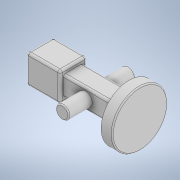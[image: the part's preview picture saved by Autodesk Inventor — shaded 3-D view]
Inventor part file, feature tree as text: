
AUTODESK INVENTOR PART (.ipt)
format: ipt  version: 2021 (Build 250183000, 183)  size: 179,712 bytes
history: native  units: in
note: dims shown in document units (in); Inventor stores cm internally (conversion verified against a paired STEP export)
features: extrude x4, sketch x4, fillet x3, plane x2
ambient origin geometry x8: Origin, YZ Plane, XZ Plane, XY Plane, X Axis, Y Axis, Z Axis, Center Point
bodies: Solid1 (feature_tree)
feature tree (13):
  extrude  "Extrusion1"  Depth=0.2362in TaperAngle=0.0deg
  extrude  "Extrusion2"  Depth=0.0787in
  fillet  "Fillet1"  Radius=0.0354in
  plane  "Work Plane1"
  extrude  "Extrusion3"  Depth=0.0709in TaperAngle=0.0deg
  plane  "Work Plane2"
  extrude  "Extrusion4"  TaperAngle=0.0deg  [1 undecoded]
  fillet  "Fillet2"  Radius=0.1969in
  fillet  "Fillet3"  Radius=0.0394in
  sketch  "Sketch1"  dims[d0=0.0472in d1=0.2362in d2=0.0in]
  sketch  "Sketch3"  dims[d4=0.1181in d5=0.0787in d6=0.0354in]
  sketch  "Sketch4"  dims[d7=0.0354in d8=0.0709in d9=0.0in]
  sketch  "Sketch5"  dims[d10=0.0079in d11=0.0in d12=0.1969in d13=0.0394in d14=0.0in d15=0.0in d16=0.0945in d17=0.1024in d18=0.1181in d19=0.0in d20=0.0079in d21=0.0039in]
note: 1 required parameter value undecoded (feature->parameter linkage not recoverable at this tier; creation-order binding heuristic only, values carry confidence <= 0.55)
